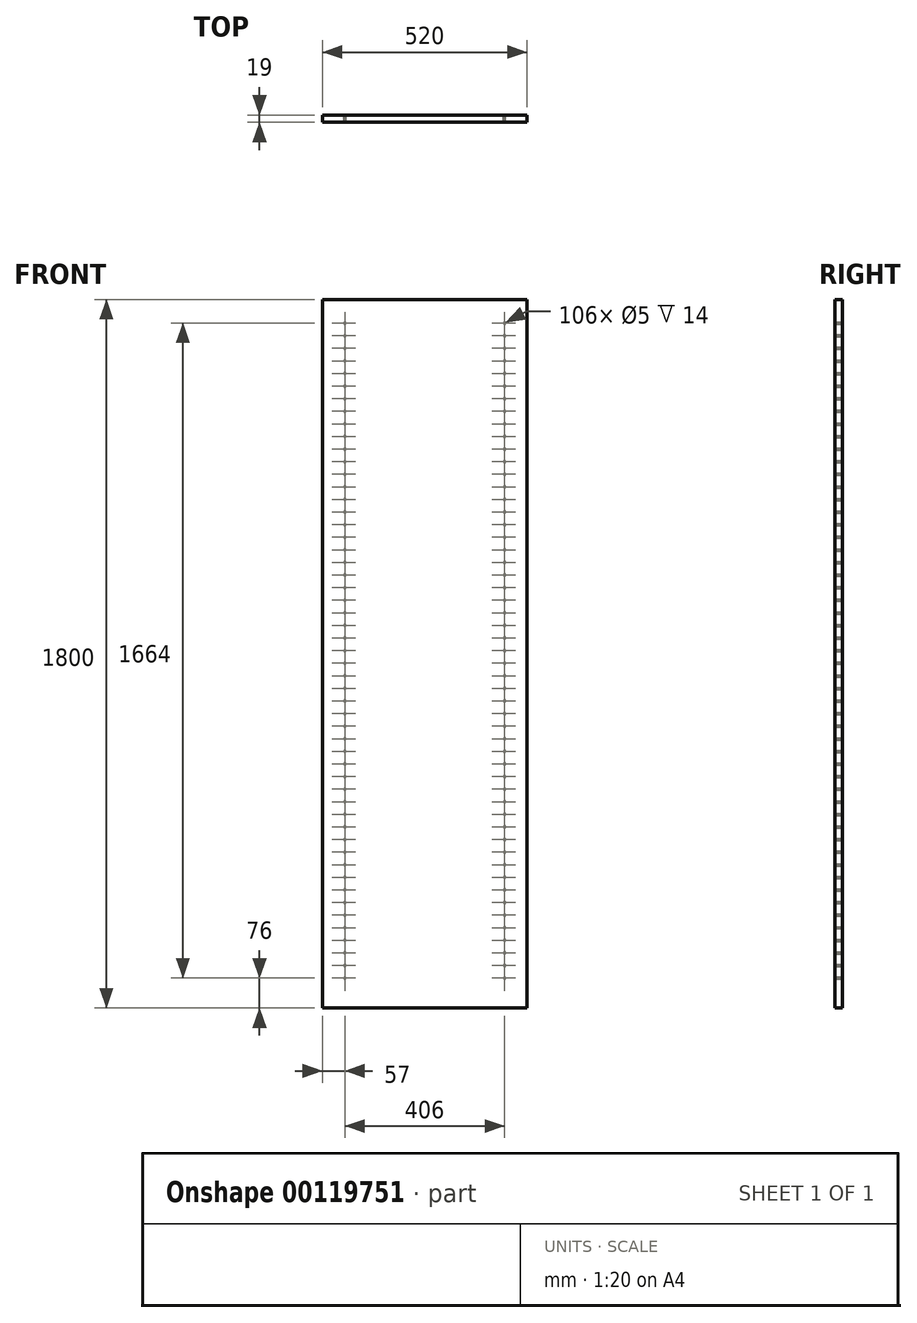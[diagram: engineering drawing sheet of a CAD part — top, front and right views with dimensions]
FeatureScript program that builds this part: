
annotation { "Feature Type Name" : "Feature", "Feature Type Description" : "" }
export const myFeature = defineFeature(function(context is Context, id is Id, definition is map)
    precondition{}
    {
        {
            var Q0;
            Q0=qCreatedBy(makeId("Front.planeOp"),FACE);
            var sketch = newSketch(context, id + "F0", { "sketchPlane" : qUnion([Q0])});
            skLineSegment(sketch, "E0.bottom", {"start": v(-260, 900) * mm, "end": v(260, 900) * mm});
            skLineSegment(sketch, "E0.top", {"start": v(-260, -900) * mm, "end": v(260, -900) * mm});
            skLineSegment(sketch, "E0.left", {"start": v(-260, 900) * mm, "end": v(-260, -900) * mm});
            skLineSegment(sketch, "E0.right", {"start": v(260, 900) * mm, "end": v(260, -900) * mm});
            skPoint(sketch, "E0.middle", {"position": v(0, 0) * mm});
            skSolve(sketch);
        }
        {
            var Q0;
            Q0=makeQuery(id+"F0.imprint","IMPRINT",FACE,{"disambiguationData":[TD([[makeQuery(id+"F0.imprint","IMPRINT",EDGE,{"derivedFrom":sQuery(id+"F0.wireOp",EDGE,"E0.bottom")}),-1.0]])]});
            extrude(context, id + "F1", {"entities" : qUnion([Q0]), "depth" : 19 * mm});
        }
        {
            var Q0;
            Q0=makeQuery(id+"F1.opExtrude","CAP_FACE",FACE,{"disambiguationData":[OSD([sQuery(id+"F0.wireOp",EDGE,"E0.bottom"),sQuery(id+"F0.wireOp",EDGE,"E0.top"),sQuery(id+"F0.wireOp",EDGE,"E0.left"),sQuery(id+"F0.wireOp",EDGE,"E0.right")])],"isStart":true});
            var sketch = newSketch(context, id + "F2", { "sketchPlane" : qUnion([Q0])});
            skCircle(sketch, "E1", {"center": v(-203, 840) * mm, "radius": 2.5 * mm});
            skCircle(sketch, "E2.0.1.0", {"center": v(-203, 808) * mm, "radius": 2.5 * mm});
            skCircle(sketch, "E2.0.2.0", {"center": v(-203, 776) * mm, "radius": 2.5 * mm});
            skCircle(sketch, "E2.0.3.0", {"center": v(-203, 744) * mm, "radius": 2.5 * mm});
            skCircle(sketch, "E2.0.4.0", {"center": v(-203, 712) * mm, "radius": 2.5 * mm});
            skCircle(sketch, "E2.0.5.0", {"center": v(-203, 680) * mm, "radius": 2.5 * mm});
            skCircle(sketch, "E2.0.6.0", {"center": v(-203, 648) * mm, "radius": 2.5 * mm});
            skCircle(sketch, "E2.0.7.0", {"center": v(-203, 616) * mm, "radius": 2.5 * mm});
            skCircle(sketch, "E2.0.8.0", {"center": v(-203, 584) * mm, "radius": 2.5 * mm});
            skCircle(sketch, "E2.0.9.0", {"center": v(-203, 552) * mm, "radius": 2.5 * mm});
            skCircle(sketch, "E2.0.10.0", {"center": v(-203, 520) * mm, "radius": 2.5 * mm});
            skCircle(sketch, "E2.0.11.0", {"center": v(-203, 488) * mm, "radius": 2.5 * mm});
            skCircle(sketch, "E2.0.12.0", {"center": v(-203, 456) * mm, "radius": 2.5 * mm});
            skCircle(sketch, "E2.0.13.0", {"center": v(-203, 424) * mm, "radius": 2.5 * mm});
            skCircle(sketch, "E2.0.14.0", {"center": v(-203, 392) * mm, "radius": 2.5 * mm});
            skCircle(sketch, "E2.0.15.0", {"center": v(-203, 360) * mm, "radius": 2.5 * mm});
            skCircle(sketch, "E2.0.16.0", {"center": v(-203, 328) * mm, "radius": 2.5 * mm});
            skCircle(sketch, "E2.0.17.0", {"center": v(-203, 296) * mm, "radius": 2.5 * mm});
            skCircle(sketch, "E2.0.18.0", {"center": v(-203, 264) * mm, "radius": 2.5 * mm});
            skCircle(sketch, "E2.0.19.0", {"center": v(-203, 232) * mm, "radius": 2.5 * mm});
            skCircle(sketch, "E2.0.20.0", {"center": v(-203, 200) * mm, "radius": 2.5 * mm});
            skCircle(sketch, "E2.0.21.0", {"center": v(-203, 168) * mm, "radius": 2.5 * mm});
            skCircle(sketch, "E2.0.22.0", {"center": v(-203, 136) * mm, "radius": 2.5 * mm});
            skCircle(sketch, "E2.0.23.0", {"center": v(-203, 104) * mm, "radius": 2.5 * mm});
            skCircle(sketch, "E2.0.24.0", {"center": v(-203, 72) * mm, "radius": 2.5 * mm});
            skCircle(sketch, "E2.0.25.0", {"center": v(-203, 40) * mm, "radius": 2.5 * mm});
            skCircle(sketch, "E2.0.26.0", {"center": v(-203, 8) * mm, "radius": 2.5 * mm});
            skCircle(sketch, "E2.0.27.0", {"center": v(-203, -24) * mm, "radius": 2.5 * mm});
            skCircle(sketch, "E2.0.28.0", {"center": v(-203, -56) * mm, "radius": 2.5 * mm});
            skCircle(sketch, "E2.0.29.0", {"center": v(-203, -88) * mm, "radius": 2.5 * mm});
            skCircle(sketch, "E2.0.30.0", {"center": v(-203, -120) * mm, "radius": 2.5 * mm});
            skCircle(sketch, "E2.0.31.0", {"center": v(-203, -152) * mm, "radius": 2.5 * mm});
            skCircle(sketch, "E2.0.32.0", {"center": v(-203, -184) * mm, "radius": 2.5 * mm});
            skCircle(sketch, "E2.0.33.0", {"center": v(-203, -216) * mm, "radius": 2.5 * mm});
            skCircle(sketch, "E2.0.34.0", {"center": v(-203, -248) * mm, "radius": 2.5 * mm});
            skCircle(sketch, "E2.0.35.0", {"center": v(-203, -280) * mm, "radius": 2.5 * mm});
            skCircle(sketch, "E2.0.36.0", {"center": v(-203, -312) * mm, "radius": 2.5 * mm});
            skCircle(sketch, "E2.0.37.0", {"center": v(-203, -344) * mm, "radius": 2.5 * mm});
            skCircle(sketch, "E2.0.38.0", {"center": v(-203, -376) * mm, "radius": 2.5 * mm});
            skCircle(sketch, "E2.0.39.0", {"center": v(-203, -408) * mm, "radius": 2.5 * mm});
            skCircle(sketch, "E2.0.40.0", {"center": v(-203, -440) * mm, "radius": 2.5 * mm});
            skCircle(sketch, "E2.0.41.0", {"center": v(-203, -472) * mm, "radius": 2.5 * mm});
            skCircle(sketch, "E2.0.42.0", {"center": v(-203, -504) * mm, "radius": 2.5 * mm});
            skCircle(sketch, "E2.0.43.0", {"center": v(-203, -536) * mm, "radius": 2.5 * mm});
            skCircle(sketch, "E2.0.44.0", {"center": v(-203, -568) * mm, "radius": 2.5 * mm});
            skCircle(sketch, "E2.0.45.0", {"center": v(-203, -600) * mm, "radius": 2.5 * mm});
            skCircle(sketch, "E2.0.46.0", {"center": v(-203, -632) * mm, "radius": 2.5 * mm});
            skCircle(sketch, "E2.0.47.0", {"center": v(-203, -664) * mm, "radius": 2.5 * mm});
            skCircle(sketch, "E2.0.48.0", {"center": v(-203, -696) * mm, "radius": 2.5 * mm});
            skCircle(sketch, "E2.0.49.0", {"center": v(-203, -728) * mm, "radius": 2.5 * mm});
            skCircle(sketch, "E2.1.0.0", {"center": v(203, 840) * mm, "radius": 2.5 * mm});
            skCircle(sketch, "E2.1.1.0", {"center": v(203, 808) * mm, "radius": 2.5 * mm});
            skCircle(sketch, "E2.1.2.0", {"center": v(203, 776) * mm, "radius": 2.5 * mm});
            skCircle(sketch, "E2.1.3.0", {"center": v(203, 744) * mm, "radius": 2.5 * mm});
            skCircle(sketch, "E2.1.4.0", {"center": v(203, 712) * mm, "radius": 2.5 * mm});
            skCircle(sketch, "E2.1.5.0", {"center": v(203, 680) * mm, "radius": 2.5 * mm});
            skCircle(sketch, "E2.1.6.0", {"center": v(203, 648) * mm, "radius": 2.5 * mm});
            skCircle(sketch, "E2.1.7.0", {"center": v(203, 616) * mm, "radius": 2.5 * mm});
            skCircle(sketch, "E2.1.8.0", {"center": v(203, 584) * mm, "radius": 2.5 * mm});
            skCircle(sketch, "E2.1.9.0", {"center": v(203, 552) * mm, "radius": 2.5 * mm});
            skCircle(sketch, "E2.1.10.0", {"center": v(203, 520) * mm, "radius": 2.5 * mm});
            skCircle(sketch, "E2.1.11.0", {"center": v(203, 488) * mm, "radius": 2.5 * mm});
            skCircle(sketch, "E2.1.12.0", {"center": v(203, 456) * mm, "radius": 2.5 * mm});
            skCircle(sketch, "E2.1.13.0", {"center": v(203, 424) * mm, "radius": 2.5 * mm});
            skCircle(sketch, "E2.1.14.0", {"center": v(203, 392) * mm, "radius": 2.5 * mm});
            skCircle(sketch, "E2.1.15.0", {"center": v(203, 360) * mm, "radius": 2.5 * mm});
            skCircle(sketch, "E2.1.16.0", {"center": v(203, 328) * mm, "radius": 2.5 * mm});
            skCircle(sketch, "E2.1.17.0", {"center": v(203, 296) * mm, "radius": 2.5 * mm});
            skCircle(sketch, "E2.1.18.0", {"center": v(203, 264) * mm, "radius": 2.5 * mm});
            skCircle(sketch, "E2.1.19.0", {"center": v(203, 232) * mm, "radius": 2.5 * mm});
            skCircle(sketch, "E2.1.20.0", {"center": v(203, 200) * mm, "radius": 2.5 * mm});
            skCircle(sketch, "E2.1.21.0", {"center": v(203, 168) * mm, "radius": 2.5 * mm});
            skCircle(sketch, "E2.1.22.0", {"center": v(203, 136) * mm, "radius": 2.5 * mm});
            skCircle(sketch, "E2.1.23.0", {"center": v(203, 104) * mm, "radius": 2.5 * mm});
            skCircle(sketch, "E2.1.24.0", {"center": v(203, 72) * mm, "radius": 2.5 * mm});
            skCircle(sketch, "E2.1.25.0", {"center": v(203, 40) * mm, "radius": 2.5 * mm});
            skCircle(sketch, "E2.1.26.0", {"center": v(203, 8) * mm, "radius": 2.5 * mm});
            skCircle(sketch, "E2.1.27.0", {"center": v(203, -24) * mm, "radius": 2.5 * mm});
            skCircle(sketch, "E2.1.28.0", {"center": v(203, -56) * mm, "radius": 2.5 * mm});
            skCircle(sketch, "E2.1.29.0", {"center": v(203, -88) * mm, "radius": 2.5 * mm});
            skCircle(sketch, "E2.1.30.0", {"center": v(203, -120) * mm, "radius": 2.5 * mm});
            skCircle(sketch, "E2.1.31.0", {"center": v(203, -152) * mm, "radius": 2.5 * mm});
            skCircle(sketch, "E2.1.32.0", {"center": v(203, -184) * mm, "radius": 2.5 * mm});
            skCircle(sketch, "E2.1.33.0", {"center": v(203, -216) * mm, "radius": 2.5 * mm});
            skCircle(sketch, "E2.1.34.0", {"center": v(203, -248) * mm, "radius": 2.5 * mm});
            skCircle(sketch, "E2.1.35.0", {"center": v(203, -280) * mm, "radius": 2.5 * mm});
            skCircle(sketch, "E2.1.36.0", {"center": v(203, -312) * mm, "radius": 2.5 * mm});
            skCircle(sketch, "E2.1.37.0", {"center": v(203, -344) * mm, "radius": 2.5 * mm});
            skCircle(sketch, "E2.1.38.0", {"center": v(203, -376) * mm, "radius": 2.5 * mm});
            skCircle(sketch, "E2.1.39.0", {"center": v(203, -408) * mm, "radius": 2.5 * mm});
            skCircle(sketch, "E2.1.40.0", {"center": v(203, -440) * mm, "radius": 2.5 * mm});
            skCircle(sketch, "E2.1.41.0", {"center": v(203, -472) * mm, "radius": 2.5 * mm});
            skCircle(sketch, "E2.1.42.0", {"center": v(203, -504) * mm, "radius": 2.5 * mm});
            skCircle(sketch, "E2.1.43.0", {"center": v(203, -536) * mm, "radius": 2.5 * mm});
            skCircle(sketch, "E2.1.44.0", {"center": v(203, -568) * mm, "radius": 2.5 * mm});
            skCircle(sketch, "E2.1.45.0", {"center": v(203, -600) * mm, "radius": 2.5 * mm});
            skCircle(sketch, "E2.1.46.0", {"center": v(203, -632) * mm, "radius": 2.5 * mm});
            skCircle(sketch, "E2.1.47.0", {"center": v(203, -664) * mm, "radius": 2.5 * mm});
            skCircle(sketch, "E2.1.48.0", {"center": v(203, -696) * mm, "radius": 2.5 * mm});
            skCircle(sketch, "E2.1.49.0", {"center": v(203, -728) * mm, "radius": 2.5 * mm});
            skLineSegment(sketch, "E2.direction1", {"start": v(-203, 840) * mm, "end": v(203, 840) * mm, "construction": true});
            skLineSegment(sketch, "E2.direction2", {"start": v(-203, 840) * mm, "end": v(-203, 808) * mm, "construction": true});
            skCircle(sketch, "E3.0.0.50", {"center": v(-203, -760) * mm, "radius": 2.5 * mm});
            skCircle(sketch, "E3.0.0.51", {"center": v(-203, -792) * mm, "radius": 2.5 * mm});
            skCircle(sketch, "E3.0.0.52", {"center": v(-203, -824) * mm, "radius": 2.5 * mm});
            skCircle(sketch, "E3.0.1.50", {"center": v(203, -760) * mm, "radius": 2.5 * mm});
            skCircle(sketch, "E3.0.1.51", {"center": v(203, -792) * mm, "radius": 2.5 * mm});
            skCircle(sketch, "E3.0.1.52", {"center": v(203, -824) * mm, "radius": 2.5 * mm});
            skSolve(sketch);
        }
        {
            var Q0;
            Q0 = qSketchRegion(id + "F2", true);
            extrude(context, id + "F3", {"entities" : qUnion([Q0]), "operationType" : NewBodyOperationType.REMOVE, "oppositeDirection" : true, "depth" : 14 * mm});
        }
    });
